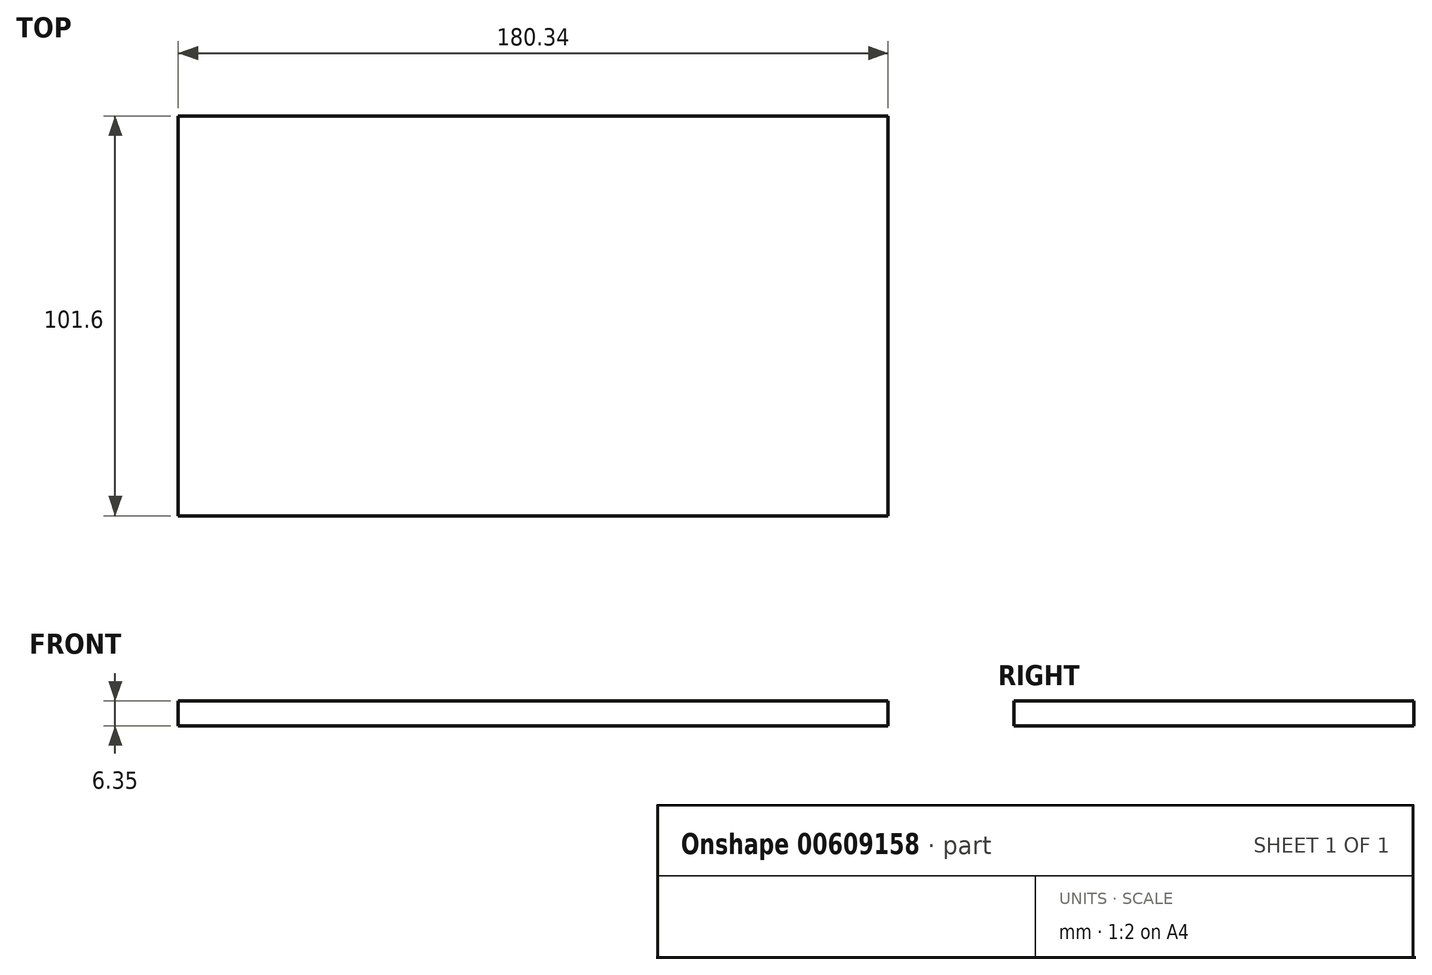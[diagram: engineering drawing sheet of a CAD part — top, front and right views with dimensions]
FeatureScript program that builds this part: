
annotation { "Feature Type Name" : "Feature", "Feature Type Description" : "" }
export const myFeature = defineFeature(function(context is Context, id is Id, definition is map)
    precondition{}
    {
        {
            var Q0;
            Q0=qCreatedBy(makeId("Top.planeOp"),FACE);
            var sketch = newSketch(context, id + "F0", { "sketchPlane" : qUnion([Q0])});
            skLineSegment(sketch, "E0.bottom", {"start": v(0, 0) * mm, "end": v(180.34, 0) * mm});
            skLineSegment(sketch, "E0.top", {"start": v(0, 101.6) * mm, "end": v(180.34, 101.6) * mm});
            skLineSegment(sketch, "E0.left", {"start": v(0, 0) * mm, "end": v(0, 101.6) * mm});
            skLineSegment(sketch, "E0.right", {"start": v(180.34, 0) * mm, "end": v(180.34, 101.6) * mm});
            skSolve(sketch);
        }
        {
            var Q0;
            Q0=makeQuery(id+"F0.imprint","IMPRINT",FACE,{"disambiguationData":[TD([[makeQuery(id+"F0.imprint","IMPRINT",EDGE,{"derivedFrom":sQuery(id+"F0.wireOp",EDGE,"E0.bottom")}),1.0]])]});
            extrude(context, id + "F1", {"entities" : qUnion([Q0]), "depth" : 6.35 * mm, "offsetDistance" : 25.4 * mm});
        }
    });
